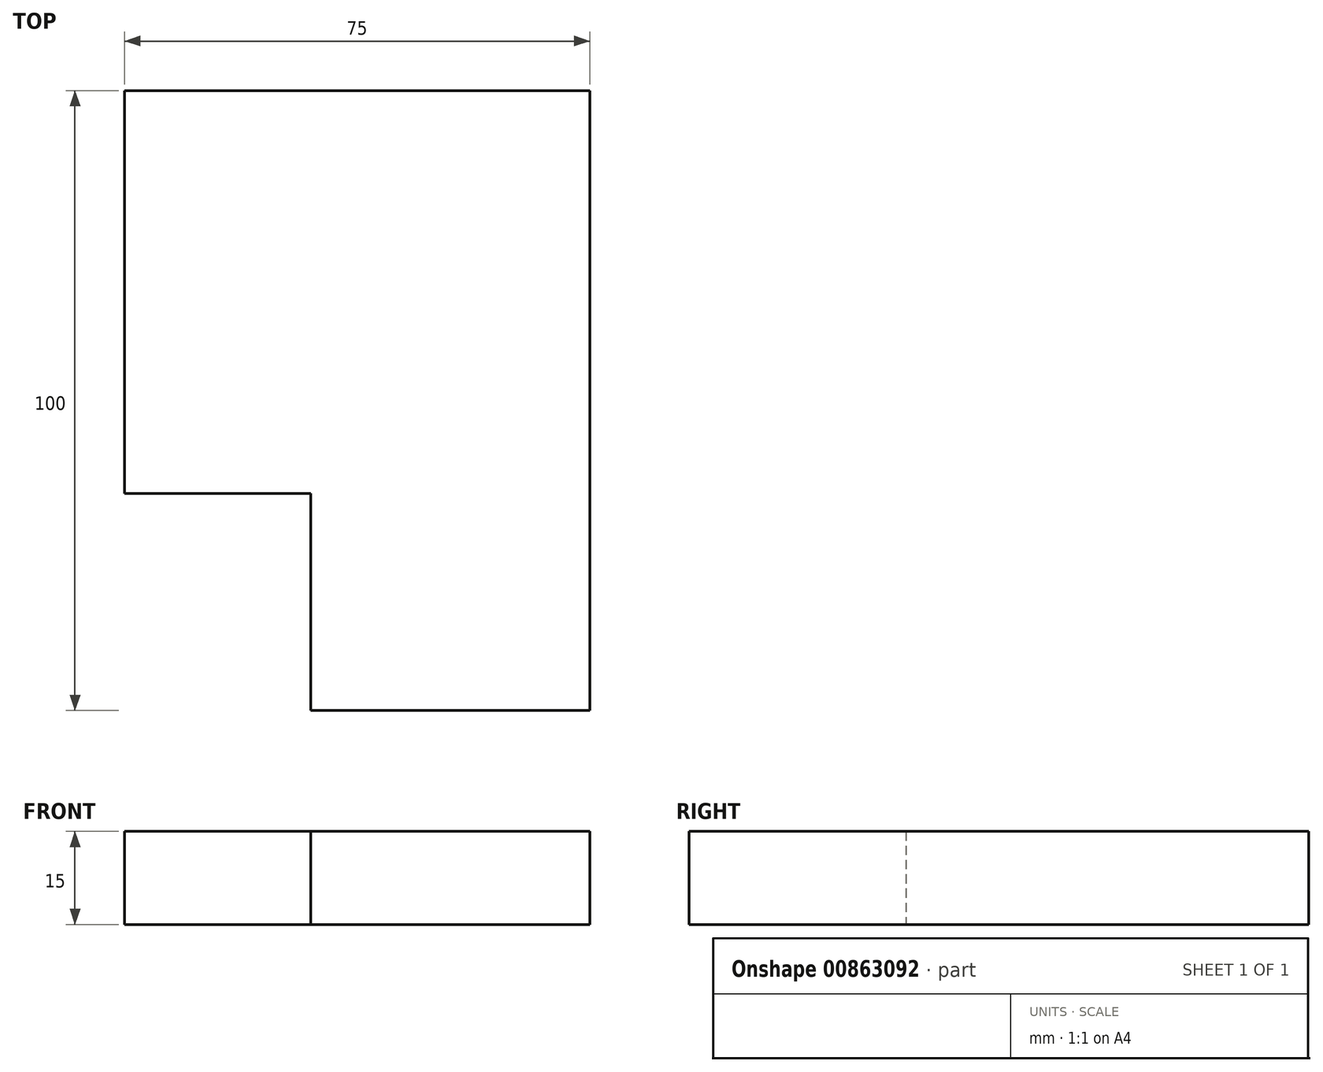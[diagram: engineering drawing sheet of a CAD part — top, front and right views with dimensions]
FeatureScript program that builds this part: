
annotation { "Feature Type Name" : "Feature", "Feature Type Description" : "" }
export const myFeature = defineFeature(function(context is Context, id is Id, definition is map)
    precondition{}
    {
        {
            var Q0;
            Q0=qCreatedBy(makeId("Top.planeOp"),FACE);
            var sketch = newSketch(context, id + "F0", { "sketchPlane" : qUnion([Q0])});
            skLineSegment(sketch, "E0.bottom", {"start": v(0, 0) * mm, "end": v(-75, 0) * mm});
            skLineSegment(sketch, "E0.top", {"start": v(0, 65) * mm, "end": v(-75, 65) * mm});
            skLineSegment(sketch, "E0.left", {"start": v(0, 0) * mm, "end": v(0, 65) * mm});
            skLineSegment(sketch, "E0.right", {"start": v(-75, 0) * mm, "end": v(-75, 65) * mm});
            skLineSegment(sketch, "E1.bottom", {"start": v(0, 0) * mm, "end": v(-45, 0) * mm});
            skLineSegment(sketch, "E1.top", {"start": v(0, -35) * mm, "end": v(-45, -35) * mm});
            skLineSegment(sketch, "E1.left", {"start": v(0, 0) * mm, "end": v(0, -35) * mm});
            skLineSegment(sketch, "E1.right", {"start": v(-45, 0) * mm, "end": v(-45, -35) * mm});
            skSolve(sketch);
        }
        {
            var Q0;
            Q0=makeQuery(id+"F0.imprint","IMPRINT",FACE,{"disambiguationData":[TD([[makeQuery(id+"F0.imprint","IMPRINT",EDGE,{"derivedFrom":sQuery(id+"F0.wireOp",EDGE,"E0.top")}),1.0]])]});
            var Q1;
            Q1=makeQuery(id+"F0.imprint","IMPRINT",FACE,{"disambiguationData":[TD([[makeQuery(id+"F0.imprint","IMPRINT",EDGE,{"derivedFrom":sQuery(id+"F0.wireOp",EDGE,"E1.top")}),-1.0]])]});
            extrude(context, id + "F1", {"entities" : qUnion([Q0, Q1]), "depth" : 15 * mm, "offsetDistance" : 25.4 * mm});
        }
    });
